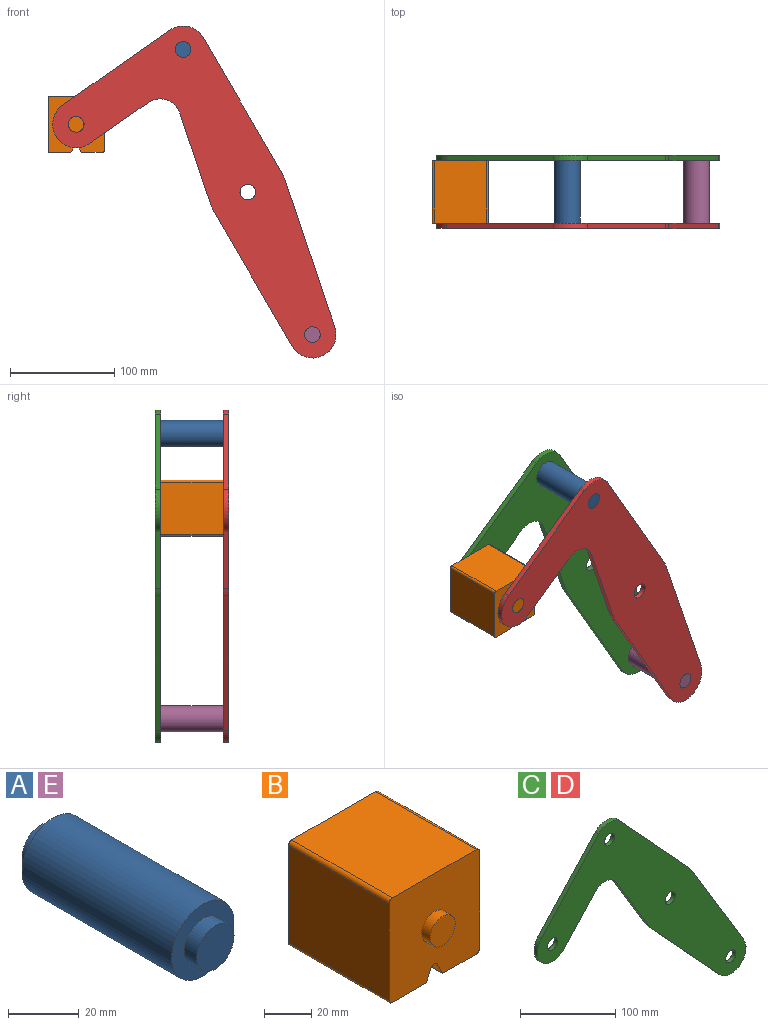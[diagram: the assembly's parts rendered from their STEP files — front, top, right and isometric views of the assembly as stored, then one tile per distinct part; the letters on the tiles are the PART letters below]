
ASSEMBLY  parts=5 mates=3
PART A: 7 faces, bbox 25x70x25 mm
  f0: cylinder r=12.5mm len=60mm, axis (0,-1,0), area 4712.4mm2, adj f2,f5
  f1: cylinder r=7.5mm len=15mm, axis (0,1,0), area 235.6mm2, adj f2,f3
  f2: plane 25x25mm, normal (0,-1,0), area 314.2mm2, adj f0,f1
  f3: plane 15x15mm, normal (0,-1,0), area 176.7mm2, adj f1
  f4: cylinder r=7.5mm len=15mm, axis (0,-1,0), area 235.6mm2, adj f5,f6
  f5: plane 25x25mm, normal (0,1,0), area 314.2mm2, adj f0,f4
  f6: plane 15x15mm, normal (0,1,0), area 176.7mm2, adj f4
PART B: 18 faces, bbox 54x70x54 mm
  f0: plane 60x50.01mm, normal (0,0,1), area 3000.4mm2, adj f4,f10,f13,f14
  f1: plane 60x50.01mm, normal (-1,0,0), area 3000.4mm2, adj f4,f10,f14,f15
  f2: plane 60x20mm, normal (0,0,-1), area 1200.2mm2, adj f3,f4,f10,f15
  f3: plane 60x6.42mm, normal (0.89,0,-0.45), area 430.8mm2, adj f2,f4,f10,f16
  f4: plane 54.01x54.01mm, normal (0,-1,0), area 2690.1mm2, adj f0,f1,f2,f3,f5,f6,f7,f9
  f5: plane 60x50.01mm, normal (1,0,0), area 3000.4mm2, adj f4,f10,f13,f17
  f6: plane 60x6.42mm, normal (-0.89,0,-0.45), area 430.8mm2, adj f4,f7,f10,f16
  f7: plane 60x20mm, normal (0,0,-1), area 1200.2mm2, adj f4,f6,f10,f17
  f8: plane 15x15mm, normal (0,-1,0), area 176.7mm2, adj f9
  f9: cylinder r=7.5mm len=15mm, axis (0,1,0), area 235.6mm2, adj f4,f8
  f10: plane 54.01x54.01mm, normal (0,1,0), area 2690.1mm2, adj f0,f1,f2,f3,f5,f6,f7,f12
  f11: plane 15x15mm, normal (0,1,0), area 176.7mm2, adj f12
  f12: cylinder r=7.5mm len=15mm, axis (0,-1,0), area 235.6mm2, adj f10,f11
  f13: cylinder r=2mm len=60mm, axis (0,-1,0), area 188.5mm2, adj f0,f4,f5,f10
  f14: cylinder r=2mm len=60mm, axis (0,1,0), area 188.5mm2, adj f0,f1,f4,f10
  f15: cylinder r=2mm len=60mm, axis (0,-1,0), area 188.5mm2, adj f1,f2,f4,f10
  f16: cylinder r=2mm len=60mm, axis (0,-1,0), area 265.7mm2, adj f3,f4,f6,f10
  f17: cylinder r=2mm len=60mm, axis (0,1,0), area 188.5mm2, adj f4,f5,f7,f10
PART C: 18 faces, bbox 309.5x5x285.1 mm
  f0: cylinder r=22.5mm len=39.07mm, axis (0,1,0), area 353.4mm2, adj f1,f13,f16,f17
  f1: plane 50.28x46.21mm, normal (0.74,0,-0.68), area 341.4mm2, adj f0,f2,f16,f17
  f2: cylinder r=20mm len=31.85mm, axis (0,1,0), area 185.5mm2, adj f1,f3,f16,f17
  f3: plane 79.23x47.81mm, normal (-0.86,0,-0.52), area 462.7mm2, adj f2,f4,f16,f17
  f4: cylinder r=37.5mm len=6mm, axis (0,1,0), area 37.6mm2, adj f3,f5,f16,f17
  f5: plane 109.88x101mm, normal (-0.74,0,-0.68), area 746.2mm2, adj f4,f6,f16,f17
  f6: cylinder r=22.5mm len=39.07mm, axis (0,1,0), area 330.9mm2, adj f5,f7,f16,f17
  f7: plane 127.78x77.11mm, normal (0.86,0,0.52), area 746.2mm2, adj f6,f8,f16,f17
  f8: cylinder r=37.5mm len=6mm, axis (0,1,0), area 37.6mm2, adj f7,f9,f16,f17
  f9: plane 109.88x101mm, normal (0.74,0,0.68), area 746.2mm2, adj f8,f10,f16,f17
  f10: cylinder r=22.5mm len=33.13mm, axis (0,1,0), area 186.2mm2, adj f9,f13,f16,f17
  f11: cylinder r=7.5mm len=15mm, axis (0,1,0), area 235.6mm2, adj f16,f17
  f12: cylinder r=7.5mm len=15mm, axis (0,1,0), area 235.6mm2, adj f16,f17
  f13: plane 92.03x84.59mm, normal (-0.74,0,0.68), area 625mm2, adj f0,f10,f16,f17
  f14: cylinder r=7.5mm len=15mm, axis (0,1,0), area 235.6mm2, adj f16,f17
  f15: cylinder r=7.5mm len=15mm, axis (0,1,0), area 235.6mm2, adj f16,f17
  f16: plane 309.5x285.07mm, normal (0,-1,0), area 24555.4mm2, adj f0,f1,f2,f3,f4,f5,f6,f7
  f17: plane 309.5x285.07mm, normal (0,1,0), area 24555.4mm2, adj f0,f1,f2,f3,f4,f5,f6,f7
PART D: same geometry as C
PART E: same geometry as A
PLACE A rot(axis=(0,1,0),12.4deg) t=(-12.3,-25.08,-1.46)mm
PLACE B t=(-2.18,-25.08,35.45)mm
PLACE C rot(axis=(0,1,0),12.4deg) t=(-12.3,39.92,-1.46)mm
PLACE D rot(axis=(0,1,0),12.4deg) t=(-12.3,-25.08,-1.46)mm
PLACE E rot(axis=(0,1,0),12.4deg) t=(111.73,-25.08,-274.63)mm
MATE fastened E.f0 <-> D.f6  axis (0,-1,0) through (49.72,-30.08,-138.04)mm
MATE fastened C.f10 <-> A.f0  axis (0,-1,0) through (-74.31,34.92,135.12)mm
MATE revolute B.f9 <-> D.f0  axis (0,-1,0) through (-176.72,-30.08,63.45)mm
